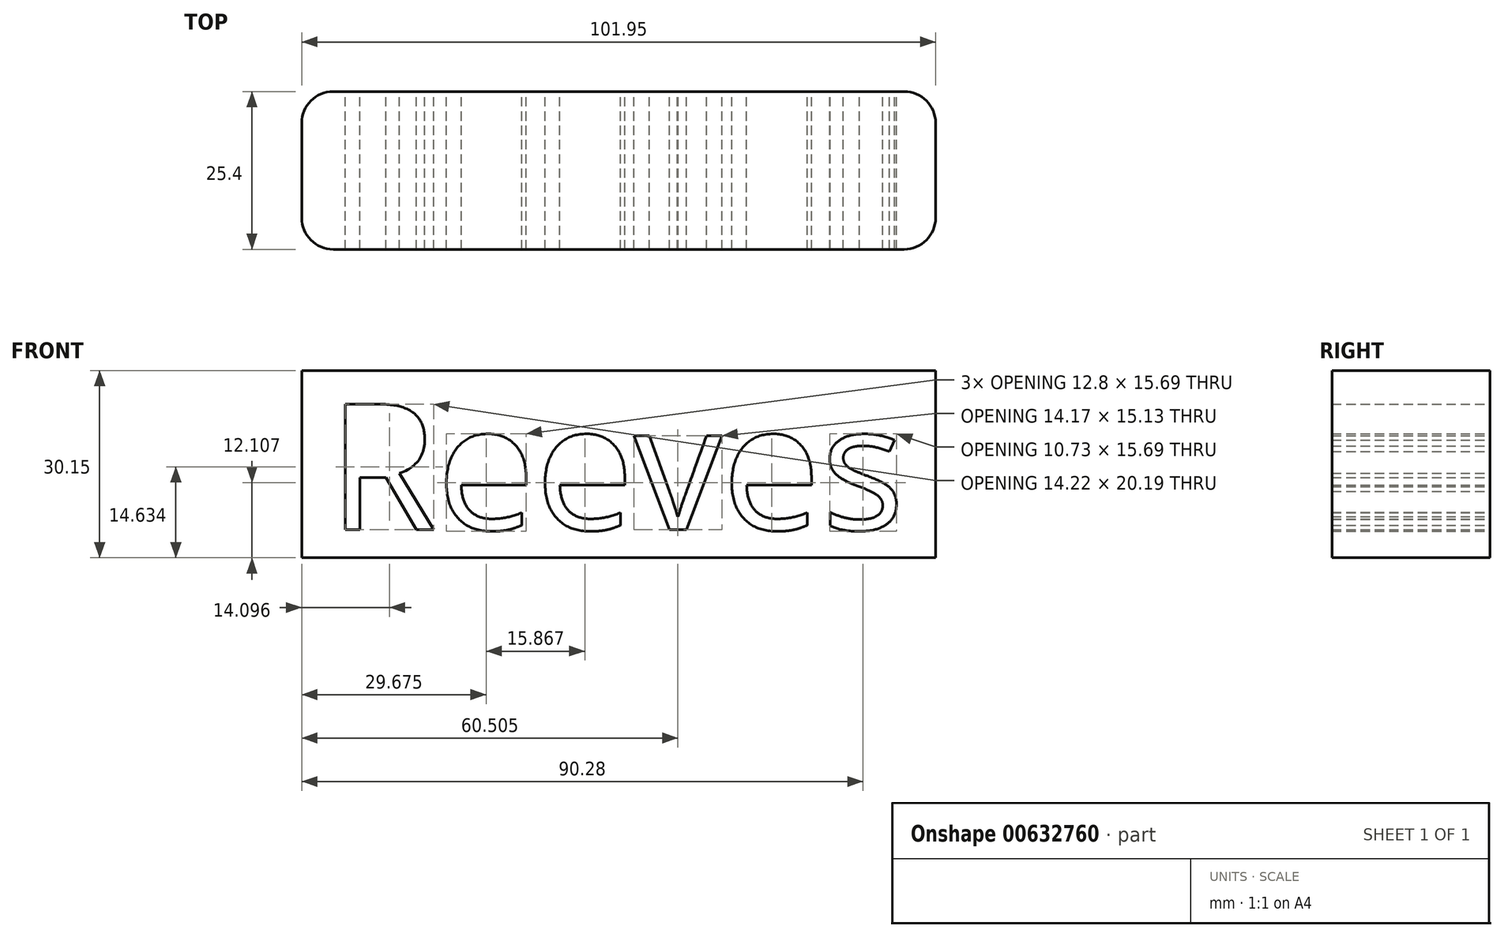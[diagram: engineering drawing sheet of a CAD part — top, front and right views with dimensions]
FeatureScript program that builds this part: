
annotation { "Feature Type Name" : "Feature", "Feature Type Description" : "" }
export const myFeature = defineFeature(function(context is Context, id is Id, definition is map)
    precondition{}
    {
        {
            var Q0;
            Q0=qCreatedBy(makeId("Front.planeOp"),FACE);
            var sketch = newSketch(context, id + "F0", { "sketchPlane" : qUnion([Q0])});
            skText(sketch, "E0", { "text": "Reeves", "fontName": "OpenSans-Regular.ttf"});
            skLineSegment(sketch, "E1.bottom", {"start": v(-37.61, 25.6) * mm, "end": v(64.34, 25.6) * mm});
            skLineSegment(sketch, "E1.top", {"start": v(-37.61, -4.54) * mm, "end": v(64.34, -4.54) * mm});
            skLineSegment(sketch, "E1.left", {"start": v(-37.61, 25.6) * mm, "end": v(-37.61, -4.54) * mm});
            skLineSegment(sketch, "E1.right", {"start": v(64.34, 25.6) * mm, "end": v(64.34, -4.54) * mm});
            const initialGuessF0  = {"E0": [-0.0334, 0, 1, 0, 0.02036]};
            skSetInitialGuess(sketch, initialGuessF0);
            skSolve(sketch);
        }
        {
            var Q0;
            Q0 = qSketchRegion(id + "F0", true);
            extrude(context, id + "F1", {"entities" : qUnion([Q0]), "depth" : 25.4 * mm, "offsetDistance" : 25.4 * mm});
        }
        {
            var Q0;
            Q0=makeQuery(id+"F1.opExtrude","CAP_EDGE",EDGE,{"disambiguationData":[OSD([sQuery(id+"F0.wireOp",EDGE,"E1.right")])],"isStart":false});
            var Q1;
            Q1=makeQuery(id+"F1.opExtrude","CAP_EDGE",EDGE,{"disambiguationData":[OSD([sQuery(id+"F0.wireOp",EDGE,"E1.left")])],"isStart":false});
            var Q2;
            Q2=makeQuery(id+"F1.opExtrude","CAP_EDGE",EDGE,{"disambiguationData":[OSD([sQuery(id+"F0.wireOp",EDGE,"E1.right")])],"isStart":true});
            var Q3;
            Q3=makeQuery(id+"F1.opExtrude","CAP_EDGE",EDGE,{"disambiguationData":[OSD([sQuery(id+"F0.wireOp",EDGE,"E1.left")])],"isStart":true});
            fillet(context, id + "F2", {"entities" : qUnion([Q0, Q1, Q2, Q3]), "radius" : 5.08 * mm, "tangentPropagation" : true, "allowEdgeOverflow" : false});
        }
    });
